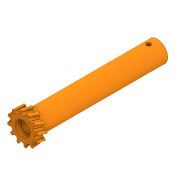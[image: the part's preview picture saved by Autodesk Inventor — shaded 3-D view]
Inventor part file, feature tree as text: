
AUTODESK INVENTOR PART (.ipt)
format: ipt  version: 2020 (Build 240168000, 168)  size: 665,088 bytes
history: native  units: in
note: dims shown in document units (in); Inventor stores cm internally (conversion verified against a paired STEP export)
features: sketch x8, extrude x4, plane x3, sweep x2, chamfer x2, projected_geometry x2, fillet x1, other x1
ambient origin geometry x8: Origin, YZ Plane, XZ Plane, XY Plane, X Axis, Y Axis, Z Axis, Center Point
bodies: Solid1 (feature_tree)
feature tree (23):
  extrude  "Extrusion1"  Depth=0.315in
  plane  "Work Plane1"
  sweep  "Sweep1"
  extrude  "Extrusion3"  Depth=0.0866in
  plane  "Work Plane2"
  extrude  "Extrusion4"  Depth=0.0787in
  plane  "Work Plane3"
  extrude  "Extrusion5"  Depth=4.7244in TaperAngle=360.0deg
  chamfer  "Chamfer1"  [1 undecoded]
  chamfer  "Chamfer2"  Distance=0.1969in
  fillet  "Fillet1"  Radius=0.0787in
  sweep  "Sweep2"
  sketch  "Sketch1"  dims[d0=0.4665in d1=0.315in]
  sketch  "Sketch3"  dims[d2=2.9921in d3=0.0in d7=-0.1969in]
  sketch  "3D Sketch1"
  other  "Helical Curve1"
  sketch  "Sketch4"  dims[d8=0.7087in d9=0.0866in]
  sketch  "Sketch5"  dims[d10=0.0787in d11=0.0787in]
  sketch  "Sketch6"  dims[d12=0.0787in d13=4.7244in d15=360.0deg]
  projected_geometry  "Projected Loop1"
  sketch  "Sketch7"  dims[d17=0.1969in d18=0.0118in d19=0.535in d20=0.0in d21=0.0in d22=0.0in d23=0.1969in d25=0.0787in d26=2.9921in d27=0.0in d28=-0.0984in d29=0.2756in d30=2.7953in d31=0.0in d32=0.1969in d33=2.9921in d34=0.0in d35=0.0591in d36=0.125in d37=0.0137in d38=0.0591in d39=0.125in d40=0.0137in d41=0.0118in d42=0.0079in d43=0.0in d44=0.0in d24=0.0344in]
  projected_geometry  "Projected Loop2"
  sketch  "3D Sketch2"
note: 1 required parameter value undecoded (feature->parameter linkage not recoverable at this tier; creation-order binding heuristic only, values carry confidence <= 0.55)
